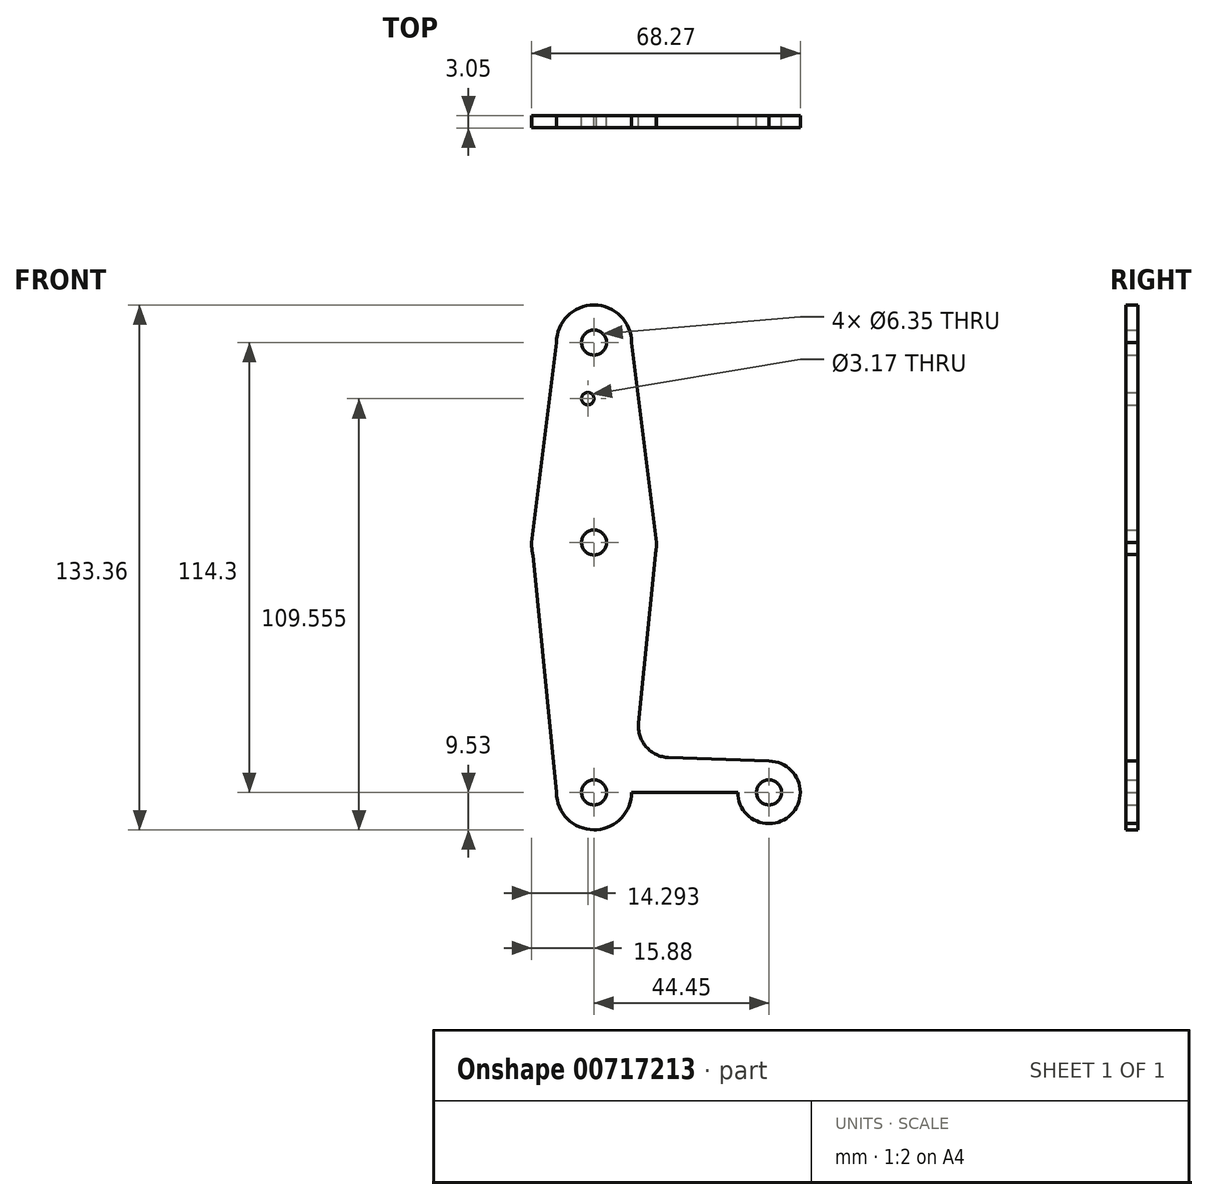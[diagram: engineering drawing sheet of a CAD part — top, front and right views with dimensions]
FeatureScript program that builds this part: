
annotation { "Feature Type Name" : "Feature", "Feature Type Description" : "" }
export const myFeature = defineFeature(function(context is Context, id is Id, definition is map)
    precondition{}
    {
        {
            var Q0;
            Q0=qCreatedBy(makeId("Front.planeOp"),FACE);
            var sketch = newSketch(context, id + "F0", { "sketchPlane" : qUnion([Q0])});
            skCircle(sketch, "E0", {"center": v(0, 0) * mm, "radius": 9.53 * mm});
            skCircle(sketch, "E1", {"center": v(44.45, 0) * mm, "radius": 7.94 * mm});
            skCircle(sketch, "E2", {"center": v(0, 63.5) * mm, "radius": 15.88 * mm});
            skCircle(sketch, "E3", {"center": v(0, 114.3) * mm, "radius": 9.53 * mm});
            skLineSegment(sketch, "E4", {"start": v(0, 114.3) * mm, "end": v(0, 0) * mm});
            skLineSegment(sketch, "E5", {"start": v(0, 0) * mm, "end": v(44.45, 0) * mm});
            skLineSegment(sketch, "E6", {"start": v(9.52, 114.3) * mm, "end": v(15.88, 63.5) * mm});
            skLineSegment(sketch, "E7", {"start": v(-9.53, 114.3) * mm, "end": v(-15.88, 63.5) * mm});
            skLineSegment(sketch, "E8", {"start": v(-15.88, 63.5) * mm, "end": v(-9.52, 0) * mm});
            skLineSegment(sketch, "E9", {"start": v(0, -9.53) * mm, "end": v(44.45, -7.94) * mm});
            skCircle(sketch, "E10", {"center": v(0, 114.3) * mm, "radius": 3.18 * mm});
            skCircle(sketch, "E11", {"center": v(0, 63.5) * mm, "radius": 3.17 * mm});
            skCircle(sketch, "E12", {"center": v(44.45, 0) * mm, "radius": 3.18 * mm});
            skCircle(sketch, "E13", {"center": v(0, 0) * mm, "radius": 3.18 * mm});
            skCircle(sketch, "E14", {"center": v(-1.59, 100.03) * mm, "radius": 1.59 * mm});
            skLineSegment(sketch, "E15", {"start": v(15.88, 63.5) * mm, "end": v(11.32, 17.58) * mm});
            skLineSegment(sketch, "E16", {"start": v(44.45, 7.94) * mm, "end": v(18.94, 8.85) * mm});
            skPoint(sketch, "E17.newPointA", {"position": v(9.57, 0) * mm});
            skArc(sketch, "E17.filletArc", {"start": v(11.32, 17.58) * mm, "mid": v(13.24, 11.57) * mm, "end": v(18.94, 8.85) * mm});
            skSolve(sketch);
        }
        {
            var Q0;
            {var subQ0=sQuery(id+"F0.wireOp",EDGE,"E8");var subQ1=sQuery(id+"F0.wireOp",EDGE,"E2");var subQ3=makeQuery(id+"F0.imprint","INTERSECT",VERTEX,{"derivedFrom":[subQ1,subQ0]});Q0=makeQuery(id+"F0.imprint","IMPRINT",FACE,{"disambiguationData":[TD([[makeQuery(id+"F0.imprint","IMPRINT",EDGE,{"disambiguationData":[TD([[subQ3,1.0]])],"derivedFrom":subQ1}),1.0]])]});}
            var Q1;
            {var subQ0=sQuery(id+"F0.wireOp",EDGE,"E15");var subQ1=sQuery(id+"F0.wireOp",EDGE,"E2");var subQ3=makeQuery(id+"F0.imprint","INTERSECT",VERTEX,{"derivedFrom":[subQ1,subQ0]});Q1=makeQuery(id+"F0.imprint","IMPRINT",FACE,{"disambiguationData":[TD([[makeQuery(id+"F0.imprint","IMPRINT",EDGE,{"disambiguationData":[TD([[subQ3,-1.0]])],"derivedFrom":subQ1}),1.0]])]});}
            var Q2;
            {var subQ0=sQuery(id+"F0.wireOp",EDGE,"E8");var subQ1=sQuery(id+"F0.wireOp",EDGE,"E0");var subQ2=makeQuery(id+"F0.imprint","INTERSECT",VERTEX,{"derivedFrom":[subQ1,subQ0]});Q2=makeQuery(id+"F0.imprint","IMPRINT",FACE,{"disambiguationData":[TD([[makeQuery(id+"F0.imprint","IMPRINT",EDGE,{"disambiguationData":[TD([[subQ2,1.0]])],"derivedFrom":subQ1}),-1.0]])]});}
            var Q3;
            {var subQ0=sQuery(id+"F0.wireOp",EDGE,"E9");var subQ1=sQuery(id+"F0.wireOp",EDGE,"E0");var subQ2=makeQuery(id+"F0.imprint","INTERSECT",VERTEX,{"disambiguationData":[OD(1.0)],"derivedFrom":[subQ1,subQ0]});Q3=makeQuery(id+"F0.imprint","IMPRINT",FACE,{"disambiguationData":[TD([[makeQuery(id+"F0.imprint","IMPRINT",EDGE,{"disambiguationData":[TD([[subQ2,-1.0]])],"derivedFrom":subQ1}),-1.0]])]});}
            var Q4;
            Q4=makeQuery(id+"F0.imprint","IMPRINT",FACE,{"disambiguationData":[TD([[makeQuery(id+"F0.imprint","IMPRINT",EDGE,{"derivedFrom":sQuery(id+"F0.wireOp",EDGE,"E12")}),-1.0]])]});
            var Q5;
            {var subQ2=sQuery(id+"F0.wireOp",EDGE,"E2");var subQ4=sQuery(id+"F0.wireOp",EDGE,"E6");var subQ5=makeQuery(id+"F0.imprint","INTERSECT",VERTEX,{"derivedFrom":[subQ2,subQ4]});Q5=makeQuery(id+"F0.imprint","IMPRINT",FACE,{"disambiguationData":[TD([[makeQuery(id+"F0.imprint","IMPRINT",EDGE,{"disambiguationData":[TD([[subQ5,-1.0]])],"derivedFrom":subQ2}),-1.0]])]});}
            var Q6;
            Q6=makeQuery(id+"F0.imprint","IMPRINT",FACE,{"disambiguationData":[TD([[makeQuery(id+"F0.imprint","IMPRINT",EDGE,{"derivedFrom":sQuery(id+"F0.wireOp",EDGE,"E10")}),-1.0]])]});
            var Q7;
            {var subQ3=sQuery(id+"F0.wireOp",EDGE,"E14");Q7=makeQuery(id+"F0.imprint","IMPRINT",FACE,{"disambiguationData":[TD([[makeQuery(id+"F0.imprint","IMPRINT",EDGE,{"derivedFrom":subQ3}),-1.0]])]});}
            var Q8;
            {var subQ8=sQuery(id+"F0.wireOp",EDGE,"E16");Q8=makeQuery(id+"F0.imprint","IMPRINT",FACE,{"disambiguationData":[TD([[makeQuery(id+"F0.imprint","IMPRINT",EDGE,{"derivedFrom":subQ8}),1.0]])]});}
            var Q9;
            {var subQ1=sQuery(id+"F0.wireOp",EDGE,"E0");var subQ10=makeQuery(id+"F0.imprint","INTERSECT",VERTEX,{"derivedFrom":[subQ1,sQuery(id+"F0.wireOp",EDGE,"E8")]});Q9=makeQuery(id+"F0.imprint","IMPRINT",FACE,{"disambiguationData":[TD([[makeQuery(id+"F0.imprint","IMPRINT",EDGE,{"disambiguationData":[TD([[subQ10,1.0]])],"derivedFrom":subQ1}),1.0]])]});}
            var Q10;
            {var subQ1=sQuery(id+"F0.wireOp",EDGE,"E2");var subQ6=sQuery(id+"F0.wireOp",EDGE,"E6");var subQ11=makeQuery(id+"F0.imprint","INTERSECT",VERTEX,{"derivedFrom":[subQ1,subQ6]});Q10=makeQuery(id+"F0.imprint","IMPRINT",FACE,{"disambiguationData":[TD([[makeQuery(id+"F0.imprint","IMPRINT",EDGE,{"disambiguationData":[TD([[subQ11,-1.0]])],"derivedFrom":subQ1}),1.0]])]});}
            var Q11;
            {var subQ1=sQuery(id+"F0.wireOp",EDGE,"E2");var subQ5=sQuery(id+"F0.wireOp",EDGE,"E7");var subQ6=makeQuery(id+"F0.imprint","INTERSECT",VERTEX,{"derivedFrom":[subQ1,subQ5]});Q11=makeQuery(id+"F0.imprint","IMPRINT",FACE,{"disambiguationData":[TD([[makeQuery(id+"F0.imprint","IMPRINT",EDGE,{"disambiguationData":[TD([[subQ6,1.0]])],"derivedFrom":subQ1}),1.0]])]});}
            var Q12;
            Q12=makeQuery(id+"FKm6zDPECtNc0PO_0.opExtrude","CAP_FACE",FACE,{"disambiguationData":[OSD([sQuery(id+"F0.wireOp",EDGE,"E0"),sQuery(id+"F0.wireOp",EDGE,"E1"),sQuery(id+"F0.wireOp",EDGE,"E2"),sQuery(id+"F0.wireOp",EDGE,"E3"),sQuery(id+"F0.wireOp",EDGE,"E4"),sQuery(id+"F0.wireOp",EDGE,"E5"),sQuery(id+"F0.wireOp",EDGE,"E6"),sQuery(id+"F0.wireOp",EDGE,"E7"),sQuery(id+"F0.wireOp",EDGE,"E8"),sQuery(id+"F0.wireOp",EDGE,"E9"),sQuery(id+"F0.wireOp",EDGE,"E10"),sQuery(id+"F0.wireOp",EDGE,"E11"),sQuery(id+"F0.wireOp",EDGE,"E12"),sQuery(id+"F0.wireOp",EDGE,"E13"),sQuery(id+"F0.wireOp",EDGE,"E14"),sQuery(id+"F0.wireOp",EDGE,"E15"),sQuery(id+"F0.wireOp",EDGE,"E16"),sQuery(id+"F0.wireOp",EDGE,"E17.filletArc")])],"isStart":true});
            var Q13;
            {var subQ0=sQuery(id+"F0.wireOp",EDGE,"E4");var subQ1=sQuery(id+"F0.wireOp",EDGE,"E0");var subQ2=makeQuery(id+"F0.imprint","INTERSECT",VERTEX,{"derivedFrom":[subQ1,subQ0]});Q13=makeQuery(id+"F0.imprint","IMPRINT",FACE,{"disambiguationData":[TD([[makeQuery(id+"F0.imprint","IMPRINT",EDGE,{"disambiguationData":[TD([[subQ2,1.0]])],"derivedFrom":subQ1}),1.0]])]});}
            extrude(context, id + "F1", {"entities" : qUnion([Q0, Q1, Q2, Q3, Q4, Q5, Q6, Q7, Q8, Q9, Q10, Q11, Q12, Q13]), "depth" : 3.05 * mm, "offsetDistance" : 25.4 * mm});
        }
    });
